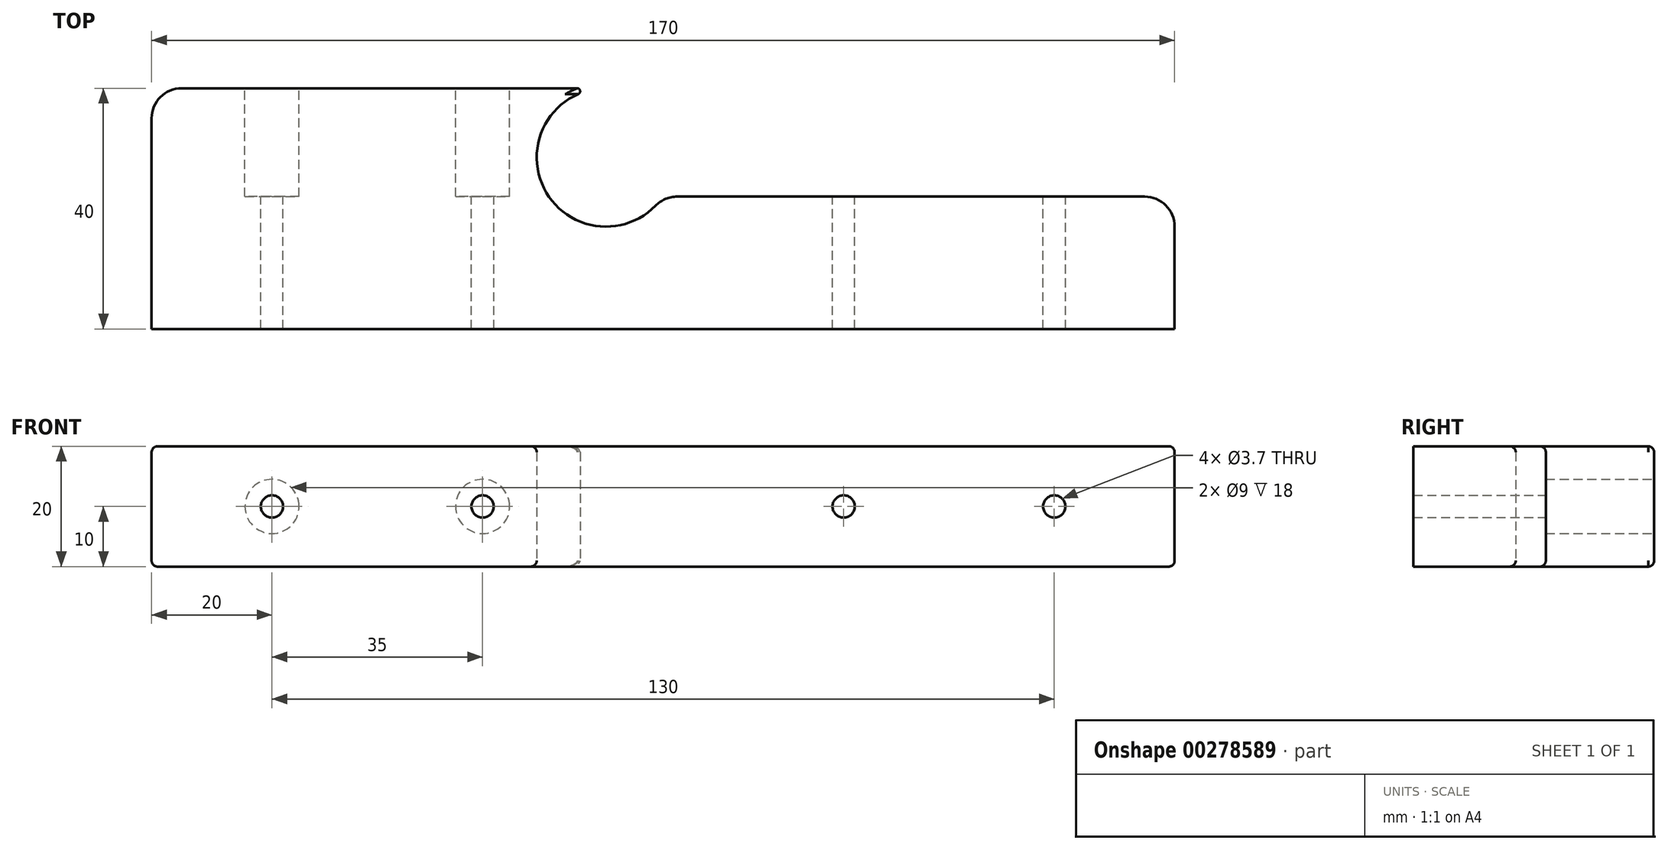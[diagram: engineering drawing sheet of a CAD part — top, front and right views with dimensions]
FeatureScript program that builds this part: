
annotation { "Feature Type Name" : "Feature", "Feature Type Description" : "" }
export const myFeature = defineFeature(function(context is Context, id is Id, definition is map)
    precondition{}
    {
        {
            var Q0;
            Q0=qCreatedBy(makeId("Top.planeOp"),FACE);
            var sketch = newSketch(context, id + "F0", { "sketchPlane" : qUnion([Q0])});
            skLineSegment(sketch, "E0.bottom", {"start": v(-80, 40) * mm, "end": v(-14.3, 40) * mm});
            skLineSegment(sketch, "E0.top", {"start": v(-85, 0) * mm, "end": v(85, 0) * mm});
            skLineSegment(sketch, "E0.left", {"start": v(-85, 35) * mm, "end": v(-85, 0) * mm});
            skLineSegment(sketch, "E0.right", {"start": v(85, 17) * mm, "end": v(85, 0) * mm});
            skLineSegment(sketch, "E1", {"start": v(2.33, 22) * mm, "end": v(80, 22) * mm});
            skArc(sketch, "E2", {"start": v(-14.1, 39.04) * mm, "mid": v(-18.96, 21.96) * mm, "end": v(-1.25, 20.48) * mm});
            skPoint(sketch, "E3.visualSharp", {"position": v(-85, 40) * mm});
            skArc(sketch, "E3.filletArc", {"start": v(-80, 40) * mm, "mid": v(-83.54, 38.54) * mm, "end": v(-85, 35) * mm});
            skPoint(sketch, "E4.visualSharp", {"position": v(85, 22) * mm});
            skArc(sketch, "E4.filletArc", {"start": v(85, 17) * mm, "mid": v(83.54, 20.54) * mm, "end": v(80, 22) * mm});
            skPoint(sketch, "E5.visualSharp", {"position": v(-9.5, 40) * mm});
            skArc(sketch, "E5.filletArc", {"start": v(-14.1, 39.04) * mm, "mid": v(-13.8, 39.6) * mm, "end": v(-14.3, 40) * mm});
            skLineSegment(sketch, "E6", {"start": v(-21, 28.5) * mm, "end": v(-21, 60.4) * mm, "construction": true});
            skArc(sketch, "E7.filletArc", {"start": v(2.33, 22) * mm, "mid": v(0.39, 21.6) * mm, "end": v(-1.25, 20.48) * mm});
            skPoint(sketch, "E8", {"position": v(65, 22) * mm});
            skPoint(sketch, "E9", {"position": v(30, 22) * mm});
            skPoint(sketch, "E10", {"position": v(-65, 40) * mm});
            skPoint(sketch, "E11", {"position": v(-30, 40) * mm});
            skLineSegment(sketch, "E12", {"start": v(-9.5, 17) * mm, "end": v(-55.82, 17) * mm, "construction": true});
            skSolve(sketch);
        }
        {
            var Q0;
            Q0 = qSketchRegion(id + "F0", true);
            extrude(context, id + "F1", {"entities" : qUnion([Q0]), "endBound" : BoundingType.SYMMETRIC, "depth" : 20 * mm});
        }
        {
            var Q0;
            Q0=makeQuery(id+"F1.opExtrude","SWEPT_FACE",FACE,{"disambiguationData":[OSD([sQuery(id+"F0.wireOp",EDGE,"E0.bottom")])]});
            var sketch = newSketch(context, id + "F2", { "sketchPlane" : qUnion([Q0])});
            skPoint(sketch, "E13", {"position": v(30, 0) * mm});
            skPoint(sketch, "E14", {"position": v(65, 0) * mm});
            skPoint(sketch, "E15", {"position": v(-30, 0) * mm});
            skPoint(sketch, "E16", {"position": v(-65, 0) * mm});
            skSolve(sketch);
        }
        {
            var Q0;
            Q0=sQuery(id+"F2.wireOp",VERTEX,"E16");
            var Q1;
            Q1=sQuery(id+"F2.wireOp",VERTEX,"E15");
            var Q2;
            Q2=makeQuery(id+"F1.opExtrude","SWEPT_BODY",BODY,{"disambiguationData":[OSD([sQuery(id+"F0.wireOp",EDGE,"E0.bottom"),sQuery(id+"F0.wireOp",EDGE,"E0.top"),sQuery(id+"F0.wireOp",EDGE,"E0.left"),sQuery(id+"F0.wireOp",EDGE,"E0.right"),sQuery(id+"F0.wireOp",EDGE,"E1"),sQuery(id+"F0.wireOp",EDGE,"E2"),sQuery(id+"F0.wireOp",EDGE,"E3.filletArc"),sQuery(id+"F0.wireOp",EDGE,"E4.filletArc"),sQuery(id+"F0.wireOp",EDGE,"E5.filletArc"),sQuery(id+"F0.wireOp",EDGE,"E7.filletArc")])]});
            hole(context, id + "F3", {"style" : HoleStyle.SIMPLE, "endStyle" : HoleEndStyle.THROUGH, "holeDiameter" : 3.7 * mm, "tappedDepth" : 12 * mm, "tapClearance" : 3, "locations" : qUnion([Q0, Q1]), "scope" : qUnion([Q2])});
        }
        {
            var Q0;
            Q0=sQuery(id+"F2.wireOp",VERTEX,"E13");
            var Q1;
            Q1=sQuery(id+"F2.wireOp",VERTEX,"E14");
            var Q2;
            Q2=makeQuery(id+"F1.opExtrude","SWEPT_BODY",BODY,{"disambiguationData":[OSD([sQuery(id+"F0.wireOp",EDGE,"E0.bottom"),sQuery(id+"F0.wireOp",EDGE,"E0.top"),sQuery(id+"F0.wireOp",EDGE,"E0.left"),sQuery(id+"F0.wireOp",EDGE,"E0.right"),sQuery(id+"F0.wireOp",EDGE,"E1"),sQuery(id+"F0.wireOp",EDGE,"E2"),sQuery(id+"F0.wireOp",EDGE,"E3.filletArc"),sQuery(id+"F0.wireOp",EDGE,"E4.filletArc"),sQuery(id+"F0.wireOp",EDGE,"E5.filletArc"),sQuery(id+"F0.wireOp",EDGE,"E7.filletArc")])]});
            hole(context, id + "F4", {"style" : HoleStyle.C_BORE, "endStyle" : HoleEndStyle.THROUGH, "holeDiameter" : 3.7 * mm, "cBoreDiameter" : 9 * mm, "cBoreDepth" : 18 * mm, "tappedDepth" : 12 * mm, "tapClearance" : 3, "locations" : qUnion([Q0, Q1]), "scope" : qUnion([Q2])});
        }
        {
            var Q0;
            Q0=makeQuery(id+"F1.opExtrude","CAP_EDGE",EDGE,{"disambiguationData":[OSD([sQuery(id+"F0.wireOp",EDGE,"E0.left")])],"isStart":false});
            var Q1;
            Q1=makeQuery(id+"F1.opExtrude","CAP_EDGE",EDGE,{"disambiguationData":[OSD([sQuery(id+"F0.wireOp",EDGE,"E0.left")])],"isStart":true});
            fillet(context, id + "F5", {"entities" : qUnion([Q0, Q1]), "radius" : 1 * mm, "tangentPropagation" : true, "allowEdgeOverflow" : false});
        }
    });
